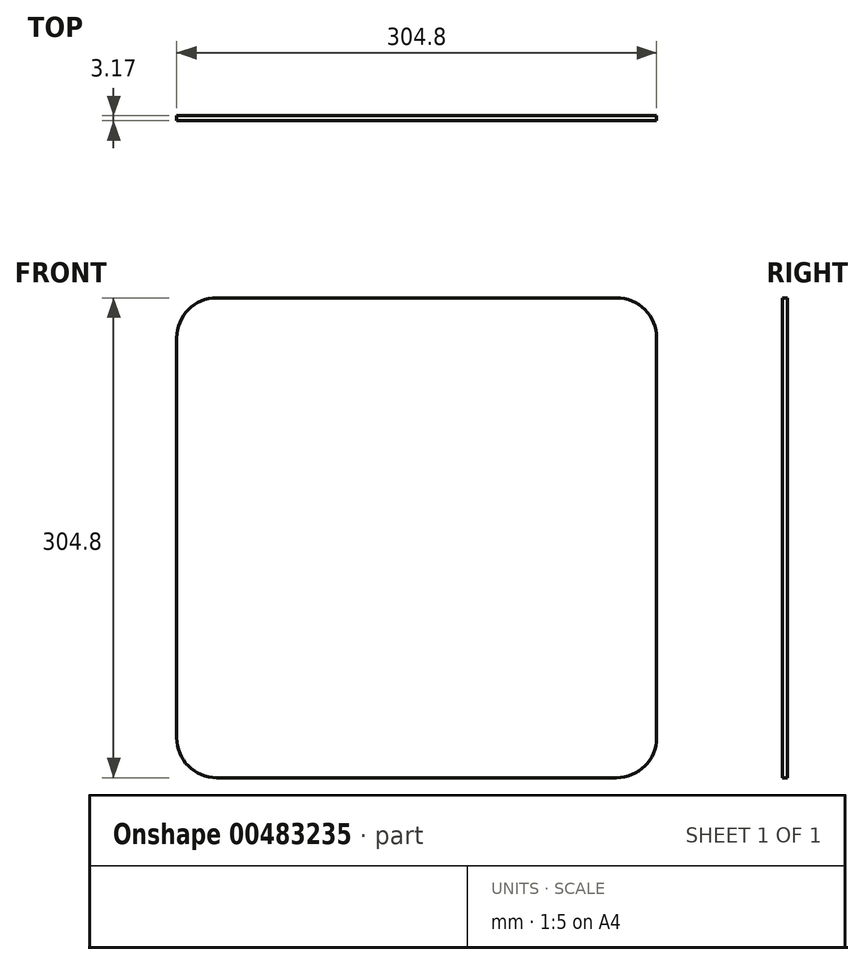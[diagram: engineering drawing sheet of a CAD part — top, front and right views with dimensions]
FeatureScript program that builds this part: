
annotation { "Feature Type Name" : "Feature", "Feature Type Description" : "" }
export const myFeature = defineFeature(function(context is Context, id is Id, definition is map)
    precondition{}
    {
        {
            var Q0;
            Q0=qCreatedBy(makeId("Front.planeOp"),FACE);
            var sketch = newSketch(context, id + "F0", { "sketchPlane" : qUnion([Q0])});
            skLineSegment(sketch, "E0.bottom", {"start": v(127, 152.4) * mm, "end": v(-127, 152.4) * mm});
            skLineSegment(sketch, "E0.top", {"start": v(127, -152.4) * mm, "end": v(-127, -152.4) * mm});
            skLineSegment(sketch, "E0.left", {"start": v(152.4, 127) * mm, "end": v(152.4, -127) * mm});
            skLineSegment(sketch, "E0.right", {"start": v(-152.4, 127) * mm, "end": v(-152.4, -127) * mm});
            skPoint(sketch, "E0.middle", {"position": v(0, 0) * mm});
            skPoint(sketch, "E1.visualSharp", {"position": v(-152.4, 152.4) * mm});
            skArc(sketch, "E1.filletArc", {"start": v(-127, 152.4) * mm, "mid": v(-144.96, 144.96) * mm, "end": v(-152.4, 127) * mm});
            skPoint(sketch, "E2.visualSharp", {"position": v(152.4, 152.4) * mm});
            skArc(sketch, "E2.filletArc", {"start": v(152.4, 127) * mm, "mid": v(144.96, 144.96) * mm, "end": v(127, 152.4) * mm});
            skPoint(sketch, "E3.visualSharp", {"position": v(152.4, -152.4) * mm});
            skArc(sketch, "E3.filletArc", {"start": v(127, -152.4) * mm, "mid": v(144.96, -144.96) * mm, "end": v(152.4, -127) * mm});
            skPoint(sketch, "E4.visualSharp", {"position": v(-152.4, -152.4) * mm});
            skArc(sketch, "E4.filletArc", {"start": v(-152.4, -127) * mm, "mid": v(-144.96, -144.96) * mm, "end": v(-127, -152.4) * mm});
            skSolve(sketch);
        }
        {
            var Q0;
            Q0 = qSketchRegion(id + "F0", true);
            extrude(context, id + "F1", {"entities" : qUnion([Q0]), "depth" : 3.17 * mm});
        }
    });
